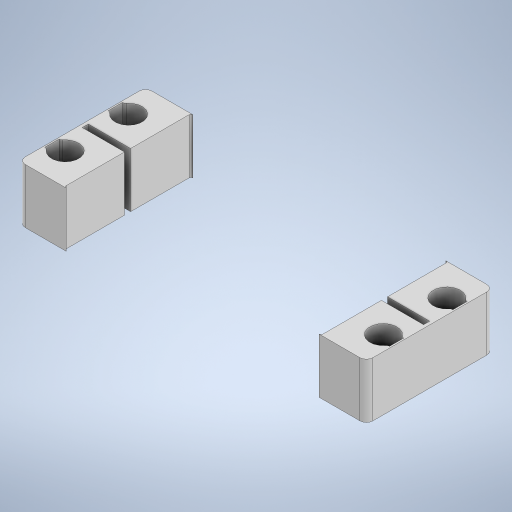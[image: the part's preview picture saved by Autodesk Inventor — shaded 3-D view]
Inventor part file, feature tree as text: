
AUTODESK INVENTOR PART (.ipt)
format: ipt  version: 2024 (Build 280153000, 153)  size: 479,232 bytes
history: native  units: mm
features: other x4, plane x2, reference x2, sketch x1, extrude x1
ambient origin geometry x8: Origin, YZ Plane, XZ Plane, XY Plane, X Axis, Y Axis, Z Axis, Center Point
bodies: Solid1 (feature_tree)
feature tree (10):
  plane  "Work Plane1"
  sketch  "Sketch2"  dims[d0=10.0mm d1=0.0mm]
  plane  "Work Plane2"
  extrude  "Extrusion1"  [1 undecoded]
  reference  "Reference3"
  reference  "Reference4"
  other  "<userpath> windows\Documents\Inventor\Robotska_roka\roka.iam"
  other  "roka.iam"
  other  "Servo Motor MG996R  With Attachments:7"
  other  "servoMotorMG996R_7"
note: 1 required parameter value undecoded (feature->parameter linkage not recoverable at this tier; creation-order binding heuristic only, values carry confidence <= 0.55)
